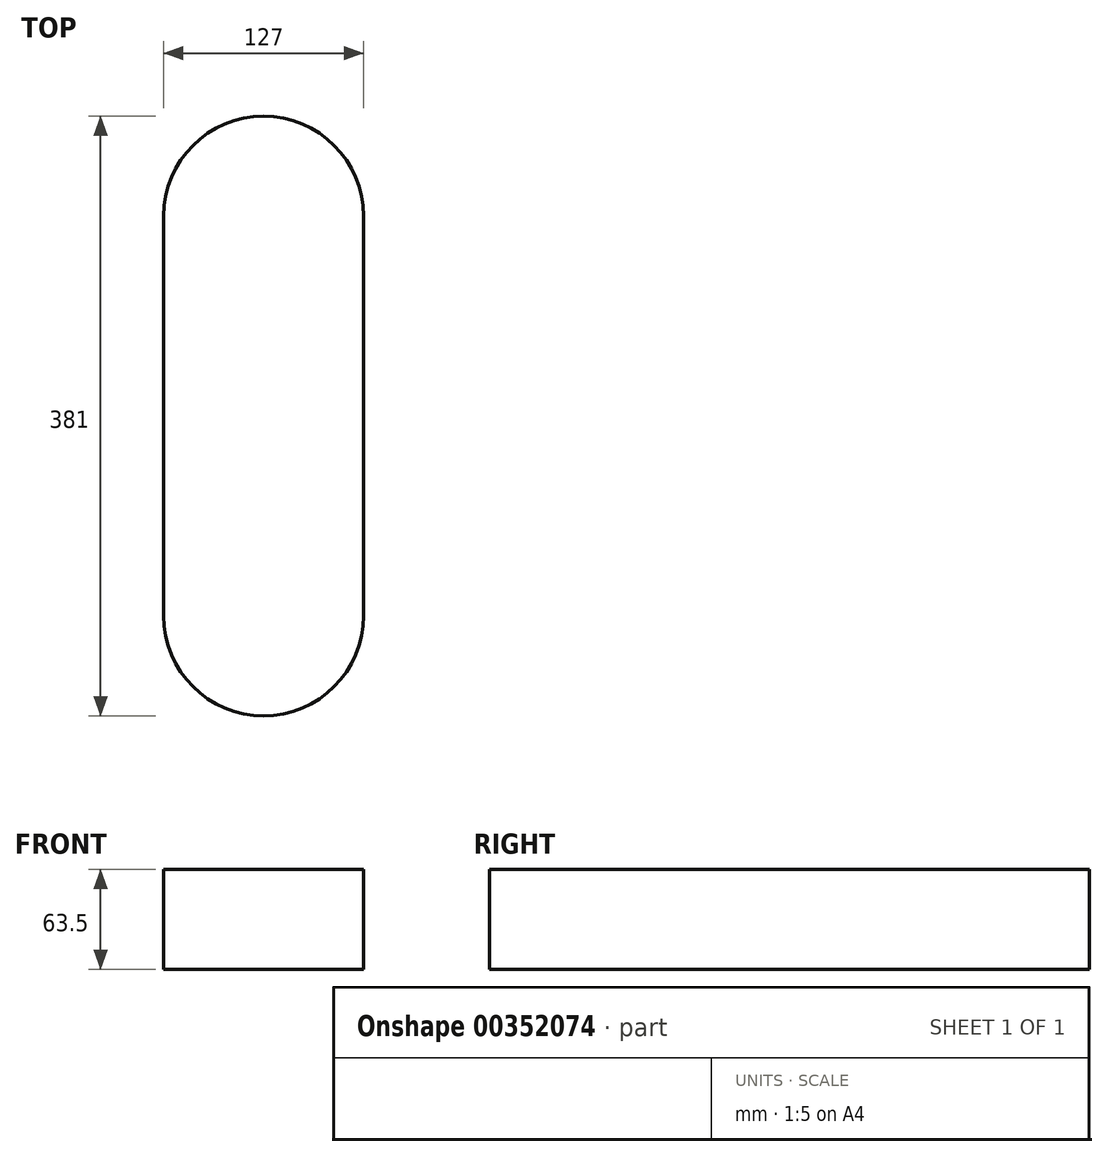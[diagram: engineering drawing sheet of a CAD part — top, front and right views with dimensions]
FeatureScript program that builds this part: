
annotation { "Feature Type Name" : "Feature", "Feature Type Description" : "" }
export const myFeature = defineFeature(function(context is Context, id is Id, definition is map)
    precondition{}
    {
        {
            var Q0;
            Q0=qCreatedBy(makeId("Top.planeOp"),FACE);
            var sketch = newSketch(context, id + "F0", { "sketchPlane" : qUnion([Q0])});
            skCircle(sketch, "E0", {"center": v(0, 0) * mm, "radius": 63.5 * mm});
            skLineSegment(sketch, "E1.bottom", {"start": v(-63.5, 0) * mm, "end": v(63.5, 0) * mm});
            skLineSegment(sketch, "E1.top", {"start": v(-63.5, -254) * mm, "end": v(63.5, -254) * mm});
            skLineSegment(sketch, "E1.left", {"start": v(-63.5, 0) * mm, "end": v(-63.5, -254) * mm});
            skLineSegment(sketch, "E1.right", {"start": v(63.5, 0) * mm, "end": v(63.5, -254) * mm});
            skCircle(sketch, "E2", {"center": v(0, -254) * mm, "radius": 63.5 * mm});
            skSolve(sketch);
        }
        {
            var Q0;
            Q0 = qSketchRegion(id + "F0", true);
            extrude(context, id + "F1", {"entities" : qUnion([Q0]), "depth" : 63.5 * mm});
        }
    });
